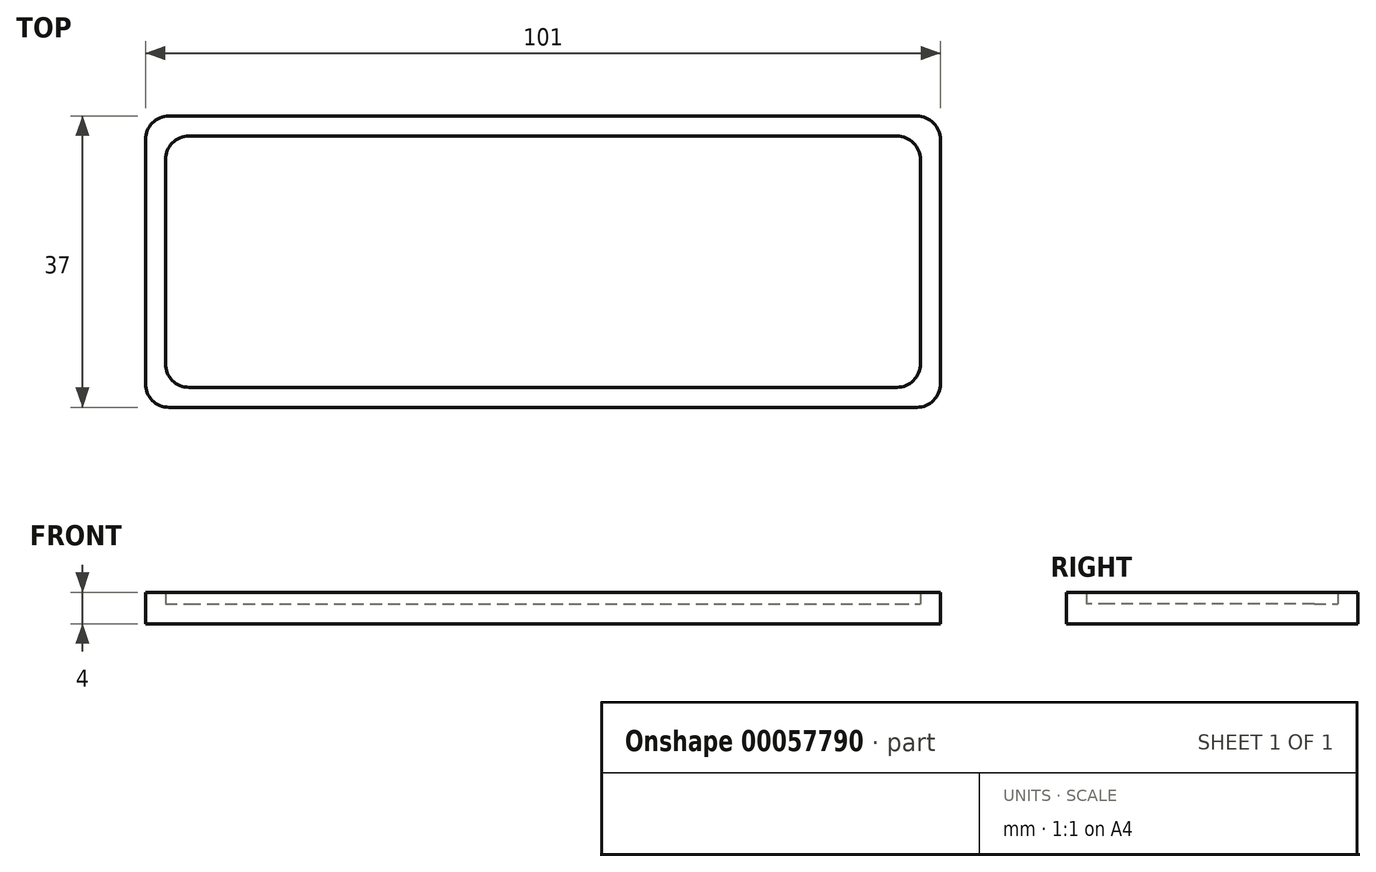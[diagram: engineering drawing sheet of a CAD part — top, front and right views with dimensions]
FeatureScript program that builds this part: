
annotation { "Feature Type Name" : "Feature", "Feature Type Description" : "" }
export const myFeature = defineFeature(function(context is Context, id is Id, definition is map)
    precondition{}
    {
        {
            var Q0;
            Q0=qCreatedBy(makeId("Top.planeOp"),FACE);
            var sketch = newSketch(context, id + "F0", { "sketchPlane" : qUnion([Q0])});
            skLineSegment(sketch, "E0.bottom", {"start": v(0, 0) * mm, "end": v(101, 0) * mm});
            skLineSegment(sketch, "E0.top", {"start": v(0, -37) * mm, "end": v(101, -37) * mm});
            skLineSegment(sketch, "E0.left", {"start": v(0, 0) * mm, "end": v(0, -37) * mm});
            skLineSegment(sketch, "E0.right", {"start": v(101, 0) * mm, "end": v(101, -37) * mm});
            skSolve(sketch);
        }
        {
            var Q0;
            Q0=makeQuery(id+"F0.imprint","IMPRINT",FACE,{"disambiguationData":[TD([[makeQuery(id+"F0.imprint","IMPRINT",EDGE,{"derivedFrom":sQuery(id+"F0.wireOp",EDGE,"E0.bottom")}),-1.0]])]});
            extrude(context, id + "F1", {"entities" : qUnion([Q0]), "depth" : 4 * mm});
        }
        {
            var Q0;
            Q0=makeQuery(id+"F1.opExtrude","CAP_FACE",FACE,{"disambiguationData":[OSD([sQuery(id+"F0.wireOp",EDGE,"E0.bottom"),sQuery(id+"F0.wireOp",EDGE,"E0.top"),sQuery(id+"F0.wireOp",EDGE,"E0.left"),sQuery(id+"F0.wireOp",EDGE,"E0.right")])],"isStart":false});
            shell(context, id + "F2", {"entities" : qUnion([Q0]), "thickness" : 2.54 * mm});
        }
        {
            var Q0;
            Q0=makeQuery(id+"F1.opExtrude","SWEPT_EDGE",EDGE,{"disambiguationData":[OSD([sQuery(id+"F0.wireOp",EDGE,"E0.bottom"),sQuery(id+"F0.wireOp",EDGE,"E0.left")])]});
            var Q1;
            Q1=makeQuery(id+"F2.opShell","OFFSET_EDGE",EDGE,{"disambiguationData":[OSD([sQuery(id+"F0.wireOp",EDGE,"E0.bottom"),sQuery(id+"F0.wireOp",EDGE,"E0.left")])]});
            var Q2;
            Q2=makeQuery(id+"F1.opExtrude","SWEPT_EDGE",EDGE,{"disambiguationData":[OSD([sQuery(id+"F0.wireOp",EDGE,"E0.bottom"),sQuery(id+"F0.wireOp",EDGE,"E0.right")])]});
            var Q3;
            Q3=makeQuery(id+"F2.opShell","OFFSET_EDGE",EDGE,{"disambiguationData":[OSD([sQuery(id+"F0.wireOp",EDGE,"E0.bottom"),sQuery(id+"F0.wireOp",EDGE,"E0.right")])]});
            var Q4;
            Q4=makeQuery(id+"F1.opExtrude","SWEPT_EDGE",EDGE,{"disambiguationData":[OSD([sQuery(id+"F0.wireOp",EDGE,"E0.top"),sQuery(id+"F0.wireOp",EDGE,"E0.right")])]});
            var Q5;
            Q5=makeQuery(id+"F2.opShell","OFFSET_EDGE",EDGE,{"disambiguationData":[OSD([sQuery(id+"F0.wireOp",EDGE,"E0.top"),sQuery(id+"F0.wireOp",EDGE,"E0.right")])]});
            var Q6;
            Q6=makeQuery(id+"F1.opExtrude","SWEPT_EDGE",EDGE,{"disambiguationData":[OSD([sQuery(id+"F0.wireOp",EDGE,"E0.top"),sQuery(id+"F0.wireOp",EDGE,"E0.left")])]});
            var Q7;
            Q7=makeQuery(id+"F2.opShell","OFFSET_EDGE",EDGE,{"disambiguationData":[OSD([sQuery(id+"F0.wireOp",EDGE,"E0.top"),sQuery(id+"F0.wireOp",EDGE,"E0.left")])]});
            fillet(context, id + "F3", {"entities" : qUnion([Q0, Q1, Q2, Q3, Q4, Q5, Q6, Q7]), "radius" : 3 * mm, "tangentPropagation" : true, "allowEdgeOverflow" : false});
        }
    });
